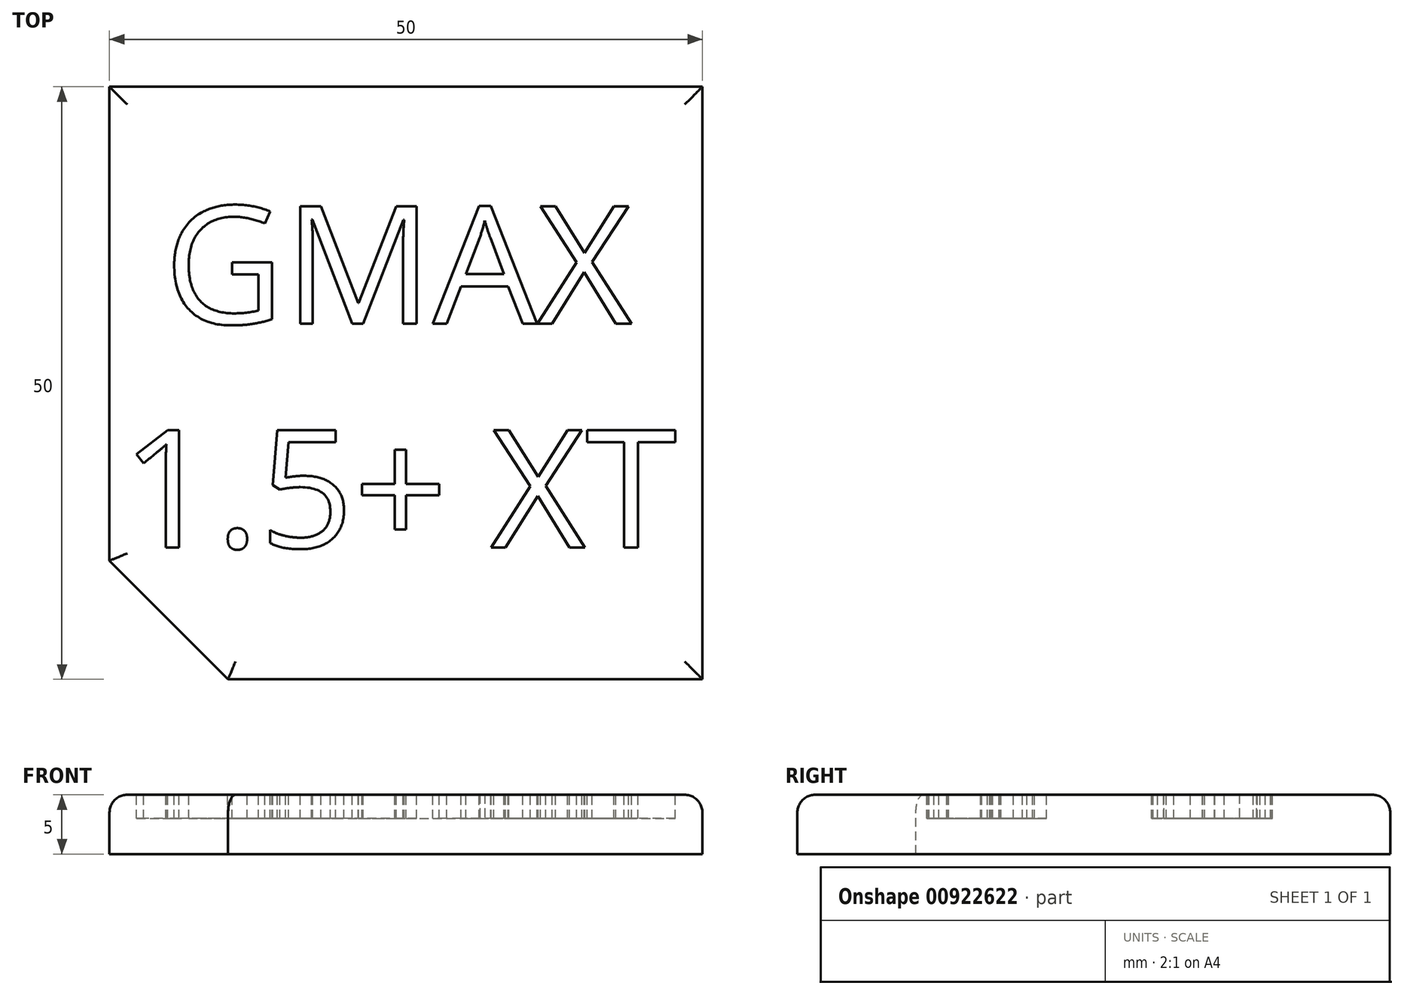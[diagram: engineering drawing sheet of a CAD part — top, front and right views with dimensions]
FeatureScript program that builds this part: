
annotation { "Feature Type Name" : "Feature", "Feature Type Description" : "" }
export const myFeature = defineFeature(function(context is Context, id is Id, definition is map)
    precondition{}
    {
        {
            var Q0;
            Q0=qCreatedBy(makeId("Top.planeOp"),FACE);
            var sketch = newSketch(context, id + "F0", { "sketchPlane" : qUnion([Q0])});
            skLineSegment(sketch, "E0.bottom", {"start": v(-25, 25) * mm, "end": v(25, 25) * mm});
            skLineSegment(sketch, "E0.top", {"start": v(-25, -25) * mm, "end": v(25, -25) * mm});
            skLineSegment(sketch, "E0.left", {"start": v(-25, 25) * mm, "end": v(-25, -25) * mm});
            skLineSegment(sketch, "E0.right", {"start": v(25, 25) * mm, "end": v(25, -25) * mm});
            skSolve(sketch);
        }
        {
            var Q0;
            Q0=makeQuery(id+"F0.imprint","IMPRINT",FACE,{"disambiguationData":[TD([[makeQuery(id+"F0.imprint","IMPRINT",EDGE,{"derivedFrom":sQuery(id+"F0.wireOp",EDGE,"E0.bottom")}),-1.0]])]});
            extrude(context, id + "F1", {"entities" : qUnion([Q0]), "depth" : 5 * mm, "offsetDistance" : 25 * mm});
        }
        {
            var Q0;
            Q0=makeQuery(id+"F1.opExtrude","CAP_FACE",FACE,{"disambiguationData":[OSD([sQuery(id+"F0.wireOp",EDGE,"E0.bottom"),sQuery(id+"F0.wireOp",EDGE,"E0.top"),sQuery(id+"F0.wireOp",EDGE,"E0.left"),sQuery(id+"F0.wireOp",EDGE,"E0.right")])],"isStart":false});
            var sketch = newSketch(context, id + "F2", { "sketchPlane" : qUnion([Q0])});
            skText(sketch, "E1", { "text": " GMAX\n1.5+ XT", "fontName": "OpenSans-Regular.ttf"});
            const initialGuessF2  = {"E1": [-0.024, 0.005, 1, 0, 0.01]};
            skSetInitialGuess(sketch, initialGuessF2);
            skSolve(sketch);
        }
        {
            var Q0;
            Q0 = qSketchRegion(id + "F2", true);
            extrude(context, id + "F3", {"entities" : qUnion([Q0]), "operationType" : NewBodyOperationType.REMOVE, "oppositeDirection" : true, "depth" : 2 * mm, "offsetDistance" : 25 * mm});
        }
        {
            var Q0;
            Q0=makeQuery(id+"F1.opExtrude","SWEPT_EDGE",EDGE,{"disambiguationData":[OSD([sQuery(id+"F0.wireOp",EDGE,"E0.top"),sQuery(id+"F0.wireOp",EDGE,"E0.left")])]});
            chamfer(context, id + "F4", {"entities" : qUnion([Q0]), "width" : 10 * mm, "tangentPropagation" : true});
        }
        {
            var Q0;
            Q0=makeQuery(id+"F1.opExtrude","CAP_EDGE",EDGE,{"disambiguationData":[OSD([sQuery(id+"F0.wireOp",EDGE,"E0.top")])],"isStart":false});
            var Q1;
            Q1=makeQuery(id+"F1.opExtrude","CAP_EDGE",EDGE,{"disambiguationData":[OSD([sQuery(id+"F0.wireOp",EDGE,"E0.right")])],"isStart":false});
            var Q2;
            Q2=makeQuery(id+"F1.opExtrude","CAP_EDGE",EDGE,{"disambiguationData":[OSD([sQuery(id+"F0.wireOp",EDGE,"E0.bottom")])],"isStart":false});
            var Q3;
            Q3=makeQuery(id+"F1.opExtrude","CAP_EDGE",EDGE,{"disambiguationData":[OSD([sQuery(id+"F0.wireOp",EDGE,"E0.left")])],"isStart":false});
            var Q4;
            {var subQ0=sQuery(id+"F0.wireOp",EDGE,"E0.top");var subQ1=sQuery(id+"F0.wireOp",EDGE,"E0.right");var subQ2=sQuery(id+"F0.wireOp",EDGE,"E0.bottom");var subQ3=sQuery(id+"F0.wireOp",EDGE,"E0.left");Q4=makeQuery(id+"F4.opChamfer","BLEND_EDGE",EDGE,{"blendedFrom":[makeQuery(id+"F1.opExtrude","SWEPT_EDGE",EDGE,{"disambiguationData":[OSD([subQ0,subQ3])]}),makeQuery(id+"F3.boolean.opBoolean","SPLIT",FACE,{"disambiguationData":[TD([makeQuery(id+"F1.opExtrude","SWEPT_FACE",FACE,{"disambiguationData":[OSD([subQ2])]})])],"derivedFrom":makeQuery(id+"F1.opExtrude","CAP_FACE",FACE,{"disambiguationData":[OSD([subQ2,subQ0,subQ3,subQ1])],"isStart":false})})],"blendedInto":[makeQuery(id+"F3.boolean.opBoolean","SPLIT",FACE,{"disambiguationData":[TD([makeQuery(id+"F1.opExtrude","SWEPT_FACE",FACE,{"disambiguationData":[OSD([subQ2])]})])],"derivedFrom":makeQuery(id+"F1.opExtrude","CAP_FACE",FACE,{"disambiguationData":[OSD([subQ2,subQ0,subQ3,subQ1])],"isStart":false})})]});}
            fillet(context, id + "F5", {"entities" : qUnion([Q0, Q1, Q2, Q3, Q4]), "radius" : 1.5 * mm, "tangentPropagation" : true, "allowEdgeOverflow" : false});
        }
    });
